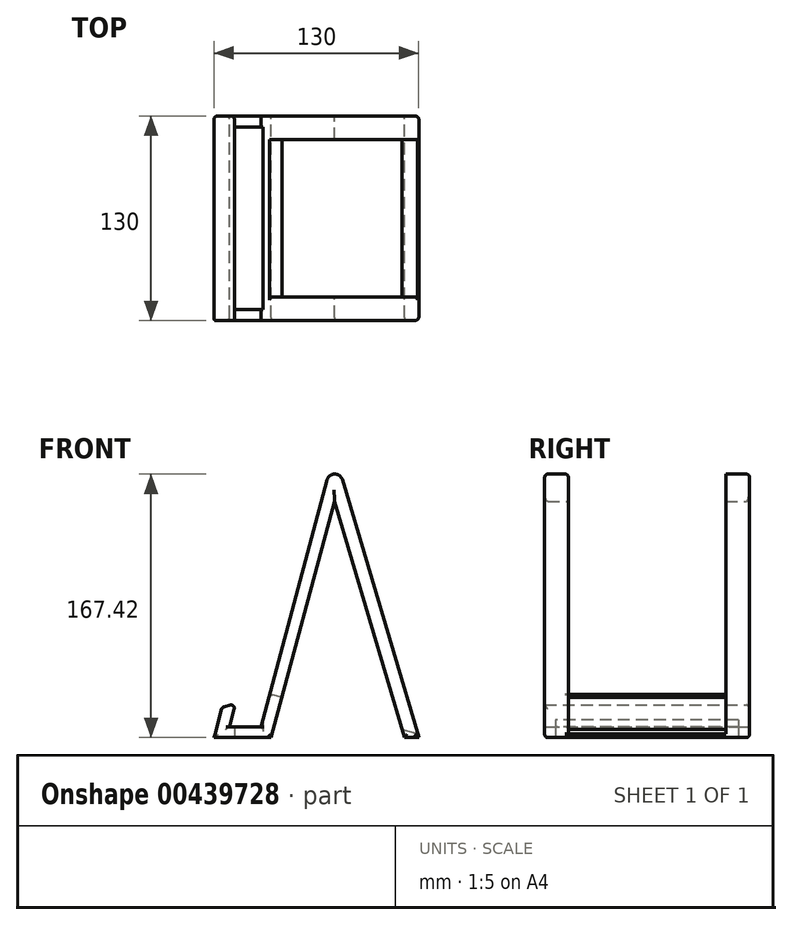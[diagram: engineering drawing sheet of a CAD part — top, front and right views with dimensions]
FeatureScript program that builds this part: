
annotation { "Feature Type Name" : "Feature", "Feature Type Description" : "" }
export const myFeature = defineFeature(function(context is Context, id is Id, definition is map)
    precondition{}
    {
        {
            var Q0;
            Q0=qCreatedBy(makeId("Front.planeOp"),FACE);
            var sketch = newSketch(context, id + "F0", { "sketchPlane" : qUnion([Q0])});
            skLineSegment(sketch, "E0", {"start": v(-66.59, -17.27) * mm, "end": v(-46.59, -17.27) * mm});
            skLineSegment(sketch, "E1", {"start": v(-46.59, -17.27) * mm, "end": v(0, 156.6) * mm});
            skLineSegment(sketch, "E2", {"start": v(-66.59, -17.27) * mm, "end": v(-62.7, -2.78) * mm});
            skLineSegment(sketch, "E3", {"start": v(0, 50.67) * mm, "end": v(0, -39.39) * mm, "construction": true});
            skLineSegment(sketch, "E4", {"start": v(-61.85, -18.45) * mm, "end": v(57.65, -18.45) * mm, "construction": true});
            skLineSegment(sketch, "E5", {"start": v(-62.26, -24.24) * mm, "end": v(59.38, -24.24) * mm, "construction": true});
            skLineSegment(sketch, "E6", {"start": v(-76.4, -24.24) * mm, "end": v(-40.2, -24.24) * mm});
            skLineSegment(sketch, "E7", {"start": v(53.6, -24.24) * mm, "end": v(44.46, -24.24) * mm});
            skLineSegment(sketch, "E8", {"start": v(-76.4, -24.24) * mm, "end": v(-71.22, -4.92) * mm});
            skLineSegment(sketch, "E9", {"start": v(-62.7, -2.78) * mm, "end": v(-71.22, -4.92) * mm});
            skLineSegment(sketch, "E10", {"start": v(0, 156.6) * mm, "end": v(53.6, -24.24) * mm});
            skLineSegment(sketch, "E11", {"start": v(44.46, -24.24) * mm, "end": v(0, 125.77) * mm});
            skLineSegment(sketch, "E12", {"start": v(0, 125.77) * mm, "end": v(-40.2, -24.24) * mm});
            skSolve(sketch);
        }
        {
            var Q0;
            Q0=makeQuery(id+"F0.imprint","IMPRINT",FACE,{"disambiguationData":[TD([[makeQuery(id+"F0.imprint","IMPRINT",EDGE,{"derivedFrom":sQuery(id+"F0.wireOp",EDGE,"E0")}),-1.0]])]});
            extrude(context, id + "F1", {"entities" : qUnion([Q0]), "depth" : 130 * mm});
        }
        {
            var Q0;
            Q0=makeQuery(id+"F1.opExtrude","CAP_EDGE",EDGE,{"disambiguationData":[OSD([sQuery(id+"F0.wireOp",EDGE,"E1")])],"isStart":false});
            var Q1;
            Q1=makeQuery(id+"F1.opExtrude","CAP_EDGE",EDGE,{"disambiguationData":[OSD([sQuery(id+"F0.wireOp",EDGE,"E12")])],"isStart":false});
            var Q2;
            Q2=makeQuery(id+"F1.opExtrude","CAP_EDGE",EDGE,{"disambiguationData":[OSD([sQuery(id+"F0.wireOp",EDGE,"E2")])],"isStart":false});
            var Q3;
            Q3=makeQuery(id+"F1.opExtrude","SWEPT_EDGE",EDGE,{"disambiguationData":[OSD([sQuery(id+"F0.wireOp",EDGE,"E2"),sQuery(id+"F0.wireOp",EDGE,"E9")])]});
            var Q4;
            Q4=makeQuery(id+"F1.opExtrude","SWEPT_EDGE",EDGE,{"disambiguationData":[OSD([sQuery(id+"F0.wireOp",EDGE,"E8"),sQuery(id+"F0.wireOp",EDGE,"E9")])]});
            var Q5;
            Q5=makeQuery(id+"F1.opExtrude","CAP_EDGE",EDGE,{"disambiguationData":[OSD([sQuery(id+"F0.wireOp",EDGE,"E11")])],"isStart":false});
            var Q6;
            Q6=makeQuery(id+"F1.opExtrude","CAP_EDGE",EDGE,{"disambiguationData":[OSD([sQuery(id+"F0.wireOp",EDGE,"E10")])],"isStart":false});
            var Q7;
            Q7=makeQuery(id+"FVv0xT3p266nYjQ_1.boolean.opBoolean","INTERSECT",EDGE,{"derivedFrom":[makeQuery(id+"F1.opExtrude","SWEPT_FACE",FACE,{"disambiguationData":[OSD([sQuery(id+"F0.wireOp",EDGE,"E10")])]}),makeQuery(id+"FVv0xT3p266nYjQ_1.opExtrude","SWEPT_FACE",FACE,{"disambiguationData":[OSD([sQuery(id+"Fklkh2xhS8xB5Al_1.wireOp",EDGE,"fdfd8cad-38a8-4885-a6c1-2b23a4faf105")])]})]});
            var Q8;
            Q8=makeQuery(id+"FVv0xT3p266nYjQ_1.boolean.opBoolean","INTERSECT",EDGE,{"derivedFrom":[makeQuery(id+"F1.opExtrude","SWEPT_FACE",FACE,{"disambiguationData":[OSD([sQuery(id+"F0.wireOp",EDGE,"E12")])]}),makeQuery(id+"FVv0xT3p266nYjQ_1.opExtrude","SWEPT_FACE",FACE,{"disambiguationData":[OSD([sQuery(id+"Fklkh2xhS8xB5Al_1.wireOp",EDGE,"fdfd8cad-38a8-4885-a6c1-2b23a4faf105")])]})]});
            var Q9;
            Q9=makeQuery(id+"FVv0xT3p266nYjQ_1.boolean.opBoolean","INTERSECT",EDGE,{"derivedFrom":[makeQuery(id+"F1.opExtrude","SWEPT_FACE",FACE,{"disambiguationData":[OSD([sQuery(id+"F0.wireOp",EDGE,"E11")])]}),makeQuery(id+"FVv0xT3p266nYjQ_1.opExtrude","SWEPT_FACE",FACE,{"disambiguationData":[OSD([sQuery(id+"Fklkh2xhS8xB5Al_1.wireOp",EDGE,"fdfd8cad-38a8-4885-a6c1-2b23a4faf105")])]})]});
            var Q10;
            Q10=makeQuery(id+"FVv0xT3p266nYjQ_1.boolean.opBoolean","INTERSECT",EDGE,{"derivedFrom":[makeQuery(id+"F1.opExtrude","SWEPT_FACE",FACE,{"disambiguationData":[OSD([sQuery(id+"F0.wireOp",EDGE,"E1")])]}),makeQuery(id+"FVv0xT3p266nYjQ_1.opExtrude","SWEPT_FACE",FACE,{"disambiguationData":[OSD([sQuery(id+"Fklkh2xhS8xB5Al_1.wireOp",EDGE,"fdfd8cad-38a8-4885-a6c1-2b23a4faf105")])]})]});
            var Q11;
            Q11=makeQuery(id+"F1.opExtrude","CAP_EDGE",EDGE,{"disambiguationData":[OSD([sQuery(id+"F0.wireOp",EDGE,"E1")])],"isStart":true});
            var Q12;
            Q12=makeQuery(id+"F1.opExtrude","CAP_EDGE",EDGE,{"disambiguationData":[OSD([sQuery(id+"F0.wireOp",EDGE,"E12")])],"isStart":true});
            var Q13;
            Q13=makeQuery(id+"F1.opExtrude","CAP_FACE",FACE,{"disambiguationData":[OSD([sQuery(id+"F0.wireOp",EDGE,"E0"),sQuery(id+"F0.wireOp",EDGE,"E1"),sQuery(id+"F0.wireOp",EDGE,"E2"),sQuery(id+"F0.wireOp",EDGE,"E6"),sQuery(id+"F0.wireOp",EDGE,"E7"),sQuery(id+"F0.wireOp",EDGE,"E8"),sQuery(id+"F0.wireOp",EDGE,"E9"),sQuery(id+"F0.wireOp",EDGE,"E10"),sQuery(id+"F0.wireOp",EDGE,"E11"),sQuery(id+"F0.wireOp",EDGE,"E12")])],"isStart":true});
            var Q14;
            Q14=makeQuery(id+"F1.opExtrude","CAP_EDGE",EDGE,{"disambiguationData":[OSD([sQuery(id+"F0.wireOp",EDGE,"E6")])],"isStart":false});
            var Q15;
            Q15=makeQuery(id+"F1.opExtrude","CAP_EDGE",EDGE,{"disambiguationData":[OSD([sQuery(id+"F0.wireOp",EDGE,"E7")])],"isStart":false});
            fillet(context, id + "F2", {"entities" : qUnion([Q0, Q1, Q2, Q3, Q4, Q5, Q6, Q7, Q8, Q9, Q10, Q11, Q12, Q13, Q14, Q15]), "radius" : 2 * mm, "tangentPropagation" : true, "allowEdgeOverflow" : false});
        }
        {
            var Q0;
            {var subQ0=sQuery(id+"F0.wireOp",EDGE,"E1");var subQ1=sQuery(id+"F0.wireOp",EDGE,"E10");Q0=makeQuery(id+"FVv0xT3p266nYjQ_1.boolean.opBoolean","SPLIT",EDGE,{"disambiguationData":[TD([makeQuery(id+"F1.opExtrude","CAP_FACE",FACE,{"disambiguationData":[OSD([sQuery(id+"F0.wireOp",EDGE,"E0"),subQ0,sQuery(id+"F0.wireOp",EDGE,"E2"),sQuery(id+"F0.wireOp",EDGE,"E6"),sQuery(id+"F0.wireOp",EDGE,"E7"),sQuery(id+"F0.wireOp",EDGE,"E8"),sQuery(id+"F0.wireOp",EDGE,"E9"),subQ1,sQuery(id+"F0.wireOp",EDGE,"E11"),sQuery(id+"F0.wireOp",EDGE,"E12")])],"isStart":true})])],"derivedFrom":makeQuery(id+"F1.opExtrude","SWEPT_EDGE",EDGE,{"disambiguationData":[OSD([subQ0,subQ1])]})});}
            var Q1;
            {var subQ0=sQuery(id+"F0.wireOp",EDGE,"E1");var subQ1=sQuery(id+"F0.wireOp",EDGE,"E10");Q1=makeQuery(id+"FVv0xT3p266nYjQ_1.boolean.opBoolean","SPLIT",EDGE,{"disambiguationData":[TD([makeQuery(id+"F1.opExtrude","CAP_FACE",FACE,{"disambiguationData":[OSD([sQuery(id+"F0.wireOp",EDGE,"E0"),subQ0,sQuery(id+"F0.wireOp",EDGE,"E2"),sQuery(id+"F0.wireOp",EDGE,"E6"),sQuery(id+"F0.wireOp",EDGE,"E7"),sQuery(id+"F0.wireOp",EDGE,"E8"),sQuery(id+"F0.wireOp",EDGE,"E9"),subQ1,sQuery(id+"F0.wireOp",EDGE,"E11"),sQuery(id+"F0.wireOp",EDGE,"E12")])],"isStart":false})])],"derivedFrom":makeQuery(id+"F1.opExtrude","SWEPT_EDGE",EDGE,{"disambiguationData":[OSD([subQ0,subQ1])]})});}
            fillet(context, id + "F3", {"entities" : qUnion([Q0, Q1]), "radius" : 5 * mm, "tangentPropagation" : true, "allowEdgeOverflow" : false});
        }
        {
            var Q0;
            Q0=makeQuery(id+"F1.opExtrude","SWEPT_FACE",FACE,{"disambiguationData":[OSD([sQuery(id+"F0.wireOp",EDGE,"E6")])]});
            var sketch = newSketch(context, id + "F4", { "sketchPlane" : qUnion([Q0])});
            skLineSegment(sketch, "E13.bottom", {"start": v(-63.4, 123) * mm, "end": v(-45.4, 123) * mm});
            skLineSegment(sketch, "E13.top", {"start": v(-63.4, 7) * mm, "end": v(-45.4, 7) * mm});
            skLineSegment(sketch, "E13.left", {"start": v(-63.4, 123) * mm, "end": v(-63.4, 7) * mm});
            skLineSegment(sketch, "E13.right", {"start": v(-45.4, 123) * mm, "end": v(-45.4, 7) * mm});
            skSolve(sketch);
        }
        {
            var Q0;
            Q0=makeQuery(id+"F4.imprint","IMPRINT",FACE,{"disambiguationData":[TD([[makeQuery(id+"F4.imprint","IMPRINT",EDGE,{"derivedFrom":sQuery(id+"F4.wireOp",EDGE,"E13.bottom")}),-1.0]])]});
            extrude(context, id + "F5", {"entities" : qUnion([Q0]), "operationType" : NewBodyOperationType.REMOVE, "oppositeDirection" : true, "depth" : 15 * mm});
        }
        {
            var Q0;
            Q0=makeQuery(id+"F1.opExtrude","SWEPT_FACE",FACE,{"disambiguationData":[OSD([sQuery(id+"F0.wireOp",EDGE,"E1")])]});
            var sketch = newSketch(context, id + "F6", { "sketchPlane" : qUnion([Q0])});
            skLineSegment(sketch, "E14.bottom", {"start": v(15, 145.01) * mm, "end": v(115, 145.01) * mm});
            skLineSegment(sketch, "E14.top", {"start": v(15, -7.38) * mm, "end": v(115, -7.38) * mm});
            skLineSegment(sketch, "E14.left", {"start": v(15, 145.01) * mm, "end": v(15, -7.38) * mm});
            skLineSegment(sketch, "E14.right", {"start": v(115, 145.01) * mm, "end": v(115, -7.38) * mm});
            skSolve(sketch);
        }
        {
            var Q0;
            {var subQ0=sQuery(id+"F6.wireOp",EDGE,"E14.top");Q0=makeQuery(id+"F6.imprint","IMPRINT",FACE,{"disambiguationData":[TD([[makeQuery(id+"F6.imprint","IMPRINT",EDGE,{"derivedFrom":subQ0}),1.0]])]});}
            var Q1;
            {var subQ0=sQuery(id+"F6.wireOp",EDGE,"E14.bottom");Q1=makeQuery(id+"F6.imprint","IMPRINT",FACE,{"disambiguationData":[TD([[makeQuery(id+"F6.imprint","IMPRINT",EDGE,{"derivedFrom":subQ0}),-1.0]])]});}
            var Q2;
            Q2=makeQuery(id+"F1.opExtrude","SWEPT_FACE",FACE,{"disambiguationData":[OSD([sQuery(id+"F0.wireOp",EDGE,"E10")])]});
            extrude(context, id + "F7", {"entities" : qUnion([Q0, Q1, Q2]), "operationType" : NewBodyOperationType.REMOVE, "oppositeDirection" : true, "depth" : 300 * mm});
        }
        {
            var Q0;
            Q0=makeQuery(id+"F7.boolean.opBoolean","COPY",EDGE,{"derivedFrom":makeQuery(id+"F7.opExtrude","CAP_EDGE",EDGE,{"disambiguationData":[OSD([sQuery(id+"F6.wireOp",EDGE,"E14.left")])],"isStart":true})});
            var Q1;
            {var subQ0=sQuery(id+"F0.wireOp",EDGE,"E10");Q1=makeQuery(id+"F7.boolean.opBoolean","INTERSECT",EDGE,{"derivedFrom":[makeQuery(id+"F1.opExtrude","SWEPT_FACE",FACE,{"disambiguationData":[OSD([subQ0])]}),makeQuery(id+"F7.opExtrude","SWEPT_FACE",FACE,{"disambiguationData":[OSD([sQuery(id+"F6.wireOp",EDGE,"E14.right")])]}),makeQuery(id+"F7.opExtrude","CAP_FACE",FACE,{"disambiguationData":[OSD([subQ0]),OD(0.0)],"isStart":false})]});}
            fillet(context, id + "F8", {"entities" : qUnion([Q0, Q1]), "radius" : 2 * mm, "tangentPropagation" : true, "allowEdgeOverflow" : false});
        }
    });
